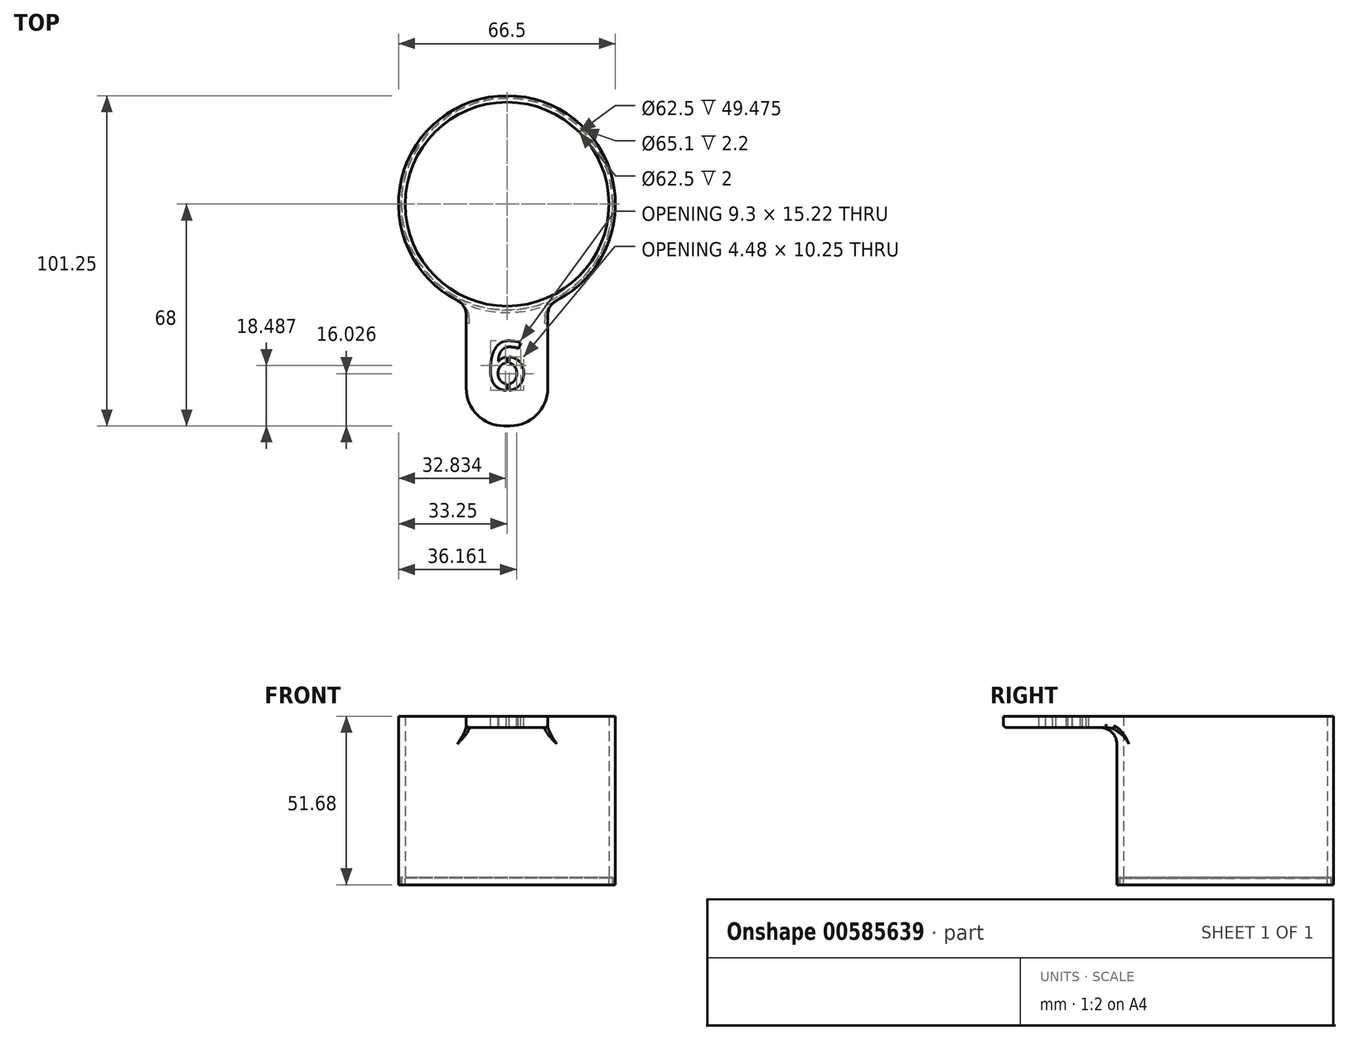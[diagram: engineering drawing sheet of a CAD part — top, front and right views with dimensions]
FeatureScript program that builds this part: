
annotation { "Feature Type Name" : "Feature", "Feature Type Description" : "" }
export const myFeature = defineFeature(function(context is Context, id is Id, definition is map)
    precondition{}
    {
        {
            var Q0;
            Q0=qCreatedBy(makeId("Top.planeOp"),FACE);
            var sketch = newSketch(context, id + "F0", { "sketchPlane" : qUnion([Q0])});
            skCircle(sketch, "E0", {"center": v(0, 0) * mm, "radius": 31.25 * mm});
            skCircle(sketch, "E1", {"center": v(0, 0) * mm, "radius": 33.25 * mm});
            skCircle(sketch, "E2", {"center": v(0, 0) * mm, "radius": 32.35 * mm});
            skSolve(sketch);
        }
        {
            var Q0;
            Q0=makeQuery(id+"F0.imprint","IMPRINT",FACE,{"disambiguationData":[TD([[makeQuery(id+"F0.imprint","IMPRINT",EDGE,{"derivedFrom":sQuery(id+"F0.wireOp",EDGE,"E0")}),1.0]])]});
            var Q1;
            Q1=makeQuery(id+"F0.imprint","IMPRINT",FACE,{"disambiguationData":[TD([[makeQuery(id+"F0.imprint","IMPRINT",EDGE,{"derivedFrom":sQuery(id+"F0.wireOp",EDGE,"E0")}),-1.0]])]});
            extrude(context, id + "F1", {"entities" : qUnion([Q0, Q1]), "depth" : 2 * mm, "offsetDistance" : 25 * mm});
        }
        {
            var Q0;
            Q0=makeQuery(id+"F0.imprint","IMPRINT",FACE,{"disambiguationData":[TD([[makeQuery(id+"F0.imprint","IMPRINT",EDGE,{"derivedFrom":sQuery(id+"F0.wireOp",EDGE,"E0")}),-1.0]])]});
            var Q1;
            Q1=makeQuery(id+"F0.imprint","IMPRINT",FACE,{"disambiguationData":[TD([[makeQuery(id+"F0.imprint","IMPRINT",EDGE,{"derivedFrom":sQuery(id+"F0.wireOp",EDGE,"E1")}),1.0]])]});
            extrude(context, id + "F2", {"entities" : qUnion([Q0, Q1]), "depth" : 49.67 * mm + 2 * mm, "offsetDistance" : 25 * mm});
        }
        {
            var Q0;
            Q0=qCreatedBy(makeId("Front.planeOp"),FACE);
            cPlane(context, id + "F3", {"entities" : qUnion([Q0]), "cplaneType" : CPlaneType.OFFSET, "offset" : 29.2 * mm, "width" : 150 * mm, "height" : 150 * mm});
        }
        {
            var Q0;
            Q0=qCreatedBy(id+"F3.planeOp",FACE);
            var sketch = newSketch(context, id + "F4", { "sketchPlane" : qUnion([Q0])});
            skPoint(sketch, "E3.middle", {"position": v(0, 17.46) * mm});
            skLineSegment(sketch, "E4", {"start": v(0, 0) * mm, "end": v(0, 51.67) * mm, "construction": true});
            skLineSegment(sketch, "E5.bottom", {"start": v(-12.5, 51.67) * mm, "end": v(12.5, 51.67) * mm});
            skLineSegment(sketch, "E5.top", {"start": v(-12.5, 48.17) * mm, "end": v(12.5, 48.17) * mm});
            skLineSegment(sketch, "E5.left", {"start": v(-12.5, 51.67) * mm, "end": v(-12.5, 48.17) * mm});
            skLineSegment(sketch, "E5.right", {"start": v(12.5, 51.68) * mm, "end": v(12.5, 48.18) * mm});
            skPoint(sketch, "E6", {"position": v(0, 51.67) * mm});
            skPoint(sketch, "E7", {"position": v(0, 48.17) * mm});
            skSolve(sketch);
        }
        {
            var Q0;
            Q0=qSketchRegion(id+"F4",true);
            extrude(context, id + "F5", {"entities" : qUnion([Q0]), "operationType" : NewBodyOperationType.ADD, "depth" : 38.8 * mm, "offsetDistance" : 25 * mm});
        }
        {
            var Q0;
            Q0=makeQuery(id+"F5.boolean.opBoolean","MERGE",FACE,{"derivedFrom":[makeQuery(id+"F2.opExtrude","CAP_FACE",FACE,{"disambiguationData":[OSD([sQuery(id+"F0.wireOp",EDGE,"E0"),sQuery(id+"F0.wireOp",EDGE,"E1")])],"isStart":false}),makeQuery(id+"F5.opExtrude","SWEPT_FACE",FACE,{"disambiguationData":[OSD([sQuery(id+"F4.wireOp",EDGE,"E3.top")])]})]});
            var sketch = newSketch(context, id + "F6", { "sketchPlane" : qUnion([Q0])});
            skCircle(sketch, "E8.0", {"center": v(0, 0) * mm, "radius": 31.25 * mm});
            skSolve(sketch);
        }
        {
            var Q0;
            Q0=qSketchRegion(id+"F6",true);
            extrude(context, id + "F7", {"entities" : qUnion([Q0]), "operationType" : NewBodyOperationType.REMOVE, "endBound" : BoundingType.THROUGH_ALL, "oppositeDirection" : true, "depth" : 35 * mm, "offsetDistance" : 25 * mm});
        }
        {
            var Q0;
            Q0=makeQuery(id+"F1.opExtrude","SWEPT_BODY",BODY,{"disambiguationData":[OSD([sQuery(id+"F0.wireOp",EDGE,"E2")])]});
            var Q1;
            Q1=makeQuery(id+"F2.opExtrude","SWEPT_BODY",BODY,{"disambiguationData":[OSD([sQuery(id+"F0.wireOp",EDGE,"E0"),sQuery(id+"F0.wireOp",EDGE,"E1")])]});
            booleanBodies(context, id + "F8", {"operationType" : BooleanOperationType.SUBTRACTION, "tools" : qUnion([Q0]), "targets" : qUnion([Q1]), "offset" : true, "offsetAll" : true, "offsetDistance" : .2 * mm, "keepTools" : true});
        }
        {
            var Q0;
            Q0=makeQuery(id+"F5.boolean.opBoolean","INTERSECT",EDGE,{"derivedFrom":[makeQuery(id+"F2.opExtrude","SWEPT_FACE",FACE,{"disambiguationData":[OSD([sQuery(id+"F0.wireOp",EDGE,"E1")])]}),makeQuery(id+"F5.opExtrude","SWEPT_FACE",FACE,{"disambiguationData":[OSD([sQuery(id+"F4.wireOp",EDGE,"E5.right")])]})]});
            var Q1;
            Q1=makeQuery(id+"F5.boolean.opBoolean","INTERSECT",EDGE,{"derivedFrom":[makeQuery(id+"F2.opExtrude","SWEPT_FACE",FACE,{"disambiguationData":[OSD([sQuery(id+"F0.wireOp",EDGE,"E1")])]}),makeQuery(id+"F5.opExtrude","SWEPT_FACE",FACE,{"disambiguationData":[OSD([sQuery(id+"F4.wireOp",EDGE,"E5.left")])]})]});
            var Q2;
            Q2=makeQuery(id+"F5.boolean.opBoolean","INTERSECT",EDGE,{"derivedFrom":[makeQuery(id+"F2.opExtrude","SWEPT_FACE",FACE,{"disambiguationData":[OSD([sQuery(id+"F0.wireOp",EDGE,"E1")])]}),makeQuery(id+"F5.opExtrude","SWEPT_FACE",FACE,{"disambiguationData":[OSD([sQuery(id+"F4.wireOp",EDGE,"E5.top")])]})]});
            fillet(context, id + "F9", {"entities" : qUnion([Q0, Q1, Q2]), "radius" : 5 * mm, "tangentPropagation" : true, "allowEdgeOverflow" : false});
        }
        {
            var Q0;
            Q0=makeQuery(id+"F5.opExtrude","CAP_EDGE",EDGE,{"disambiguationData":[OSD([sQuery(id+"F4.wireOp",EDGE,"E5.right")])],"isStart":false});
            var Q1;
            Q1=makeQuery(id+"F5.opExtrude","CAP_EDGE",EDGE,{"disambiguationData":[OSD([sQuery(id+"F4.wireOp",EDGE,"E5.left")])],"isStart":false});
            fillet(context, id + "F10", {"entities" : qUnion([Q0, Q1]), "radius" : 11.6 * mm, "tangentPropagation" : true, "allowEdgeOverflow" : false});
        }
        {
            var Q0;
            {var subQ0=makeQuery(id+"F2.opExtrude","SWEPT_FACE",FACE,{"disambiguationData":[OSD([sQuery(id+"F0.wireOp",EDGE,"E1")])]});Q0=makeQuery(id+"F9.opFillet","BLEND_EDGE",EDGE,{"blendedFrom":[makeQuery(id+"F5.boolean.opBoolean","INTERSECT",EDGE,{"derivedFrom":[subQ0,makeQuery(id+"F5.opExtrude","SWEPT_FACE",FACE,{"disambiguationData":[OSD([sQuery(id+"F4.wireOp",EDGE,"E5.right")])]})]}),makeQuery(id+"F5.boolean.opBoolean","INTERSECT",EDGE,{"derivedFrom":[subQ0,makeQuery(id+"F5.opExtrude","SWEPT_FACE",FACE,{"disambiguationData":[OSD([sQuery(id+"F4.wireOp",EDGE,"E5.top")])]})]})],"blendedInto":[]});}
            fillet(context, id + "F11", {"entities" : qUnion([Q0]), "radius" : 1 * mm, "tangentPropagation" : true, "allowEdgeOverflow" : false});
        }
        {
            var Q0;
            Q0=makeQuery(id+"F5.boolean.opBoolean","MERGE",FACE,{"derivedFrom":[makeQuery(id+"F2.opExtrude","CAP_FACE",FACE,{"disambiguationData":[OSD([sQuery(id+"F0.wireOp",EDGE,"E0"),sQuery(id+"F0.wireOp",EDGE,"E1")])],"isStart":false}),makeQuery(id+"F5.opExtrude","SWEPT_FACE",FACE,{"disambiguationData":[OSD([sQuery(id+"F4.wireOp",EDGE,"E5.bottom")])]})]});
            var sketch = newSketch(context, id + "F12", { "sketchPlane" : qUnion([Q0])});
            skText(sketch, "E9", { "text": "6", "fontName": "AllertaStencil-Regular.ttf"});
            const initialGuessF12  = {"E9": [-0.00655, -0.057, 1, 0, 0.015]};
            skSetInitialGuess(sketch, initialGuessF12);
            skSolve(sketch);
        }
        {
            var Q0;
            Q0 = qSketchRegion(id + "F12", true);
            extrude(context, id + "F13", {"entities" : qUnion([Q0]), "operationType" : NewBodyOperationType.REMOVE, "oppositeDirection" : true, "depth" : 25 * mm, "offsetDistance" : 25 * mm});
        }
    });
